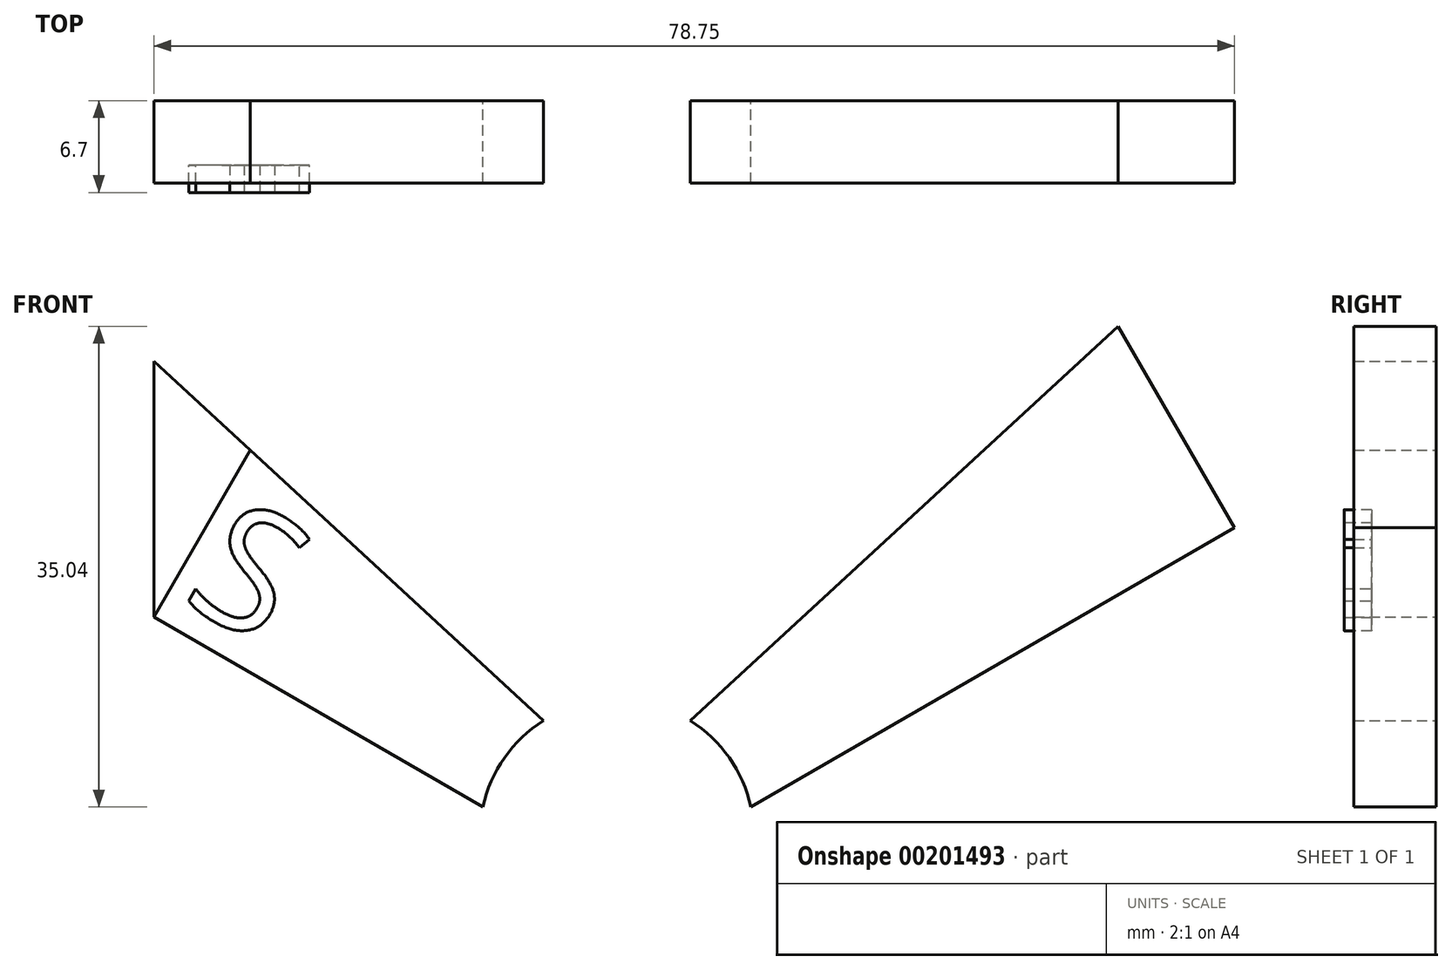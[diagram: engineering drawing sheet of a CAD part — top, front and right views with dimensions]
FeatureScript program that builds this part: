
annotation { "Feature Type Name" : "Feature", "Feature Type Description" : "" }
export const myFeature = defineFeature(function(context is Context, id is Id, definition is map)
    precondition{}
    {
        {
            var Q0;
            Q0=qCreatedBy(makeId("Front.planeOp"),FACE);
            var sketch = newSketch(context, id + "F0", { "sketchPlane" : qUnion([Q0])});
            skCircle(sketch, "E0", {"center": v(0, 0) * mm, "radius": 10 * mm});
            skLineSegment(sketch, "E1.bottom", {"start": v(45, -45) * mm, "end": v(-45, -45) * mm});
            skLineSegment(sketch, "E1.top", {"start": v(45, 45) * mm, "end": v(-45, 45) * mm});
            skLineSegment(sketch, "E1.left", {"start": v(45, -45) * mm, "end": v(45, 45) * mm});
            skLineSegment(sketch, "E1.right", {"start": v(-45, -45) * mm, "end": v(-45, 45) * mm});
            skLineSegment(sketch, "E2", {"start": v(0, 0) * mm, "end": v(-45, 45) * mm, "construction": true});
            skLineSegment(sketch, "E3", {"start": v(0, 0) * mm, "end": v(45, 45) * mm, "construction": true});
            skLineSegment(sketch, "E4", {"start": v(-45, 45) * mm, "end": v(-45, 0) * mm});
            skLineSegment(sketch, "E5", {"start": v(-45, 45) * mm, "end": v(-45, 22.5) * mm});
            skLineSegment(sketch, "E6", {"start": v(0, 0) * mm, "end": v(0, 7) * mm});
            skLineSegment(sketch, "E7", {"start": v(0, 0) * mm, "end": v(0, 3.5) * mm});
            skLineSegment(sketch, "E8", {"start": v(0, 0) * mm, "end": v(0, -3.5) * mm});
            skLineSegment(sketch, "E9", {"start": v(-45, 22.5) * mm, "end": v(0, -3.5) * mm});
            skLineSegment(sketch, "E10", {"start": v(-45, 45) * mm, "end": v(0, 3.5) * mm, "construction": true});
            skLineSegment(sketch, "E11", {"start": v(0, 3.5) * mm, "end": v(45, 45) * mm});
            skLineSegment(sketch, "E12", {"start": v(0, -3.5) * mm, "end": v(45, 22.5) * mm});
            skLineSegment(sketch, "E13", {"start": v(45, 22.5) * mm, "end": v(45, 45) * mm});
            skLineSegment(sketch, "E14", {"start": v(0, 3.5) * mm, "end": v(-45, 45) * mm});
            skLineSegment(sketch, "E15", {"start": v(0, 3.5) * mm, "end": v(-33.75, 34.62) * mm, "construction": true});
            skLineSegment(sketch, "E16", {"start": v(-33.75, 34.62) * mm, "end": v(-33.75, 16) * mm});
            skLineSegment(sketch, "E17", {"start": v(-33.75, 16) * mm, "end": v(-26.73, 28.15) * mm});
            skLineSegment(sketch, "E18", {"start": v(45, 22.5) * mm, "end": v(36.52, 37.18) * mm});
            skSolve(sketch);
        }
        {
            var Q0;
            {var subQ5=sQuery(id+"F0.wireOp",EDGE,"E17");Q0=makeQuery(id+"F0.imprint","IMPRINT",FACE,{"disambiguationData":[TD([[makeQuery(id+"F0.imprint","IMPRINT",EDGE,{"derivedFrom":subQ5}),-1.0]])]});}
            var Q1;
            {var subQ4=sQuery(id+"F0.wireOp",EDGE,"E7");Q1=makeQuery(id+"F0.imprint","IMPRINT",FACE,{"disambiguationData":[TD([[makeQuery(id+"F0.imprint","IMPRINT",EDGE,{"derivedFrom":subQ4}),1.0]])]});}
            var Q2;
            {var subQ5=sQuery(id+"F0.wireOp",EDGE,"E18");Q2=makeQuery(id+"F0.imprint","IMPRINT",FACE,{"disambiguationData":[TD([[makeQuery(id+"F0.imprint","IMPRINT",EDGE,{"derivedFrom":subQ5}),1.0]])]});}
            var Q3;
            {var subQ1=sQuery(id+"F0.wireOp",EDGE,"E7");Q3=makeQuery(id+"F0.imprint","IMPRINT",FACE,{"disambiguationData":[TD([[makeQuery(id+"F0.imprint","IMPRINT",EDGE,{"derivedFrom":subQ1}),-1.0]])]});}
            extrude(context, id + "F1", {"entities" : qUnion([Q0, Q1, Q2, Q3]), "depth" : 6 * mm});
        }
        {
            var Q0;
            Q0=makeQuery(id+"F1.opExtrude","CAP_FACE",FACE,{"disambiguationData":[OSD([sQuery(id+"F0.wireOp",EDGE,"E9"),sQuery(id+"F0.wireOp",EDGE,"E11"),sQuery(id+"F0.wireOp",EDGE,"E12"),sQuery(id+"F0.wireOp",EDGE,"E14"),sQuery(id+"F0.wireOp",EDGE,"E17"),sQuery(id+"F0.wireOp",EDGE,"E18")])],"isStart":false});
            var sketch = newSketch(context, id + "F2", { "sketchPlane" : qUnion([Q0])});
            skText(sketch, "E19", { "text": "S", "fontName": "OpenSans-Regular.ttf"});
            const initialGuessF2  = {"E19": [-0.03444, 0.01897, 1, 0, 0.009]};
            skSetInitialGuess(sketch, initialGuessF2);
            skSolve(sketch);
        }
        {
            var Q0;
            Q0 = qSketchRegion(id + "F2", true);
            extrude(context, id + "F3", {"entities" : qUnion([Q0]), "depth" : 2 * mm});
        }
        {
            var Q0;
            Q0=makeQuery(id+"F3.opExtrude","SWEPT_BODY",BODY,{"disambiguationData":[OSD([sQuery(id+"F2.wireOp",EDGE,"E19.sketch_text.stroke-0"),sQuery(id+"F2.wireOp",EDGE,"E19.sketch_text.stroke-1"),sQuery(id+"F2.wireOp",EDGE,"E19.sketch_text.stroke-2"),sQuery(id+"F2.wireOp",EDGE,"E19.sketch_text.stroke-3"),sQuery(id+"F2.wireOp",EDGE,"E19.sketch_text.stroke-4"),sQuery(id+"F2.wireOp",EDGE,"E19.sketch_text.stroke-5"),sQuery(id+"F2.wireOp",EDGE,"E19.sketch_text.stroke-6"),sQuery(id+"F2.wireOp",EDGE,"E19.sketch_text.stroke-7"),sQuery(id+"F2.wireOp",EDGE,"E19.sketch_text.stroke-8"),sQuery(id+"F2.wireOp",EDGE,"E19.sketch_text.stroke-9"),sQuery(id+"F2.wireOp",EDGE,"E19.sketch_text.stroke-10"),sQuery(id+"F2.wireOp",EDGE,"E19.sketch_text.stroke-11"),sQuery(id+"F2.wireOp",EDGE,"E19.sketch_text.stroke-12"),sQuery(id+"F2.wireOp",EDGE,"E19.sketch_text.stroke-13"),sQuery(id+"F2.wireOp",EDGE,"E19.sketch_text.stroke-14"),sQuery(id+"F2.wireOp",EDGE,"E19.sketch_text.stroke-15"),sQuery(id+"F2.wireOp",EDGE,"E19.sketch_text.stroke-16"),sQuery(id+"F2.wireOp",EDGE,"E19.sketch_text.stroke-17"),sQuery(id+"F2.wireOp",EDGE,"E19.sketch_text.stroke-18"),sQuery(id+"F2.wireOp",EDGE,"E19.sketch_text.stroke-19"),sQuery(id+"F2.wireOp",EDGE,"E19.sketch_text.stroke-20"),sQuery(id+"F2.wireOp",EDGE,"E19.sketch_text.stroke-21"),sQuery(id+"F2.wireOp",EDGE,"E19.sketch_text.stroke-22"),sQuery(id+"F2.wireOp",EDGE,"E19.sketch_text.stroke-23"),sQuery(id+"F2.wireOp",EDGE,"E19.sketch_text.stroke-24")])]});
            var Q1;
            Q1=makeQuery(id+"F1.opExtrude","SWEPT_EDGE",EDGE,{"disambiguationData":[OSD([sQuery(id+"F0.wireOp",EDGE,"E14"),sQuery(id+"F0.wireOp",EDGE,"E17")])]});
            transform(context, id + "F4", {"entities" : qUnion([Q0]), "transformType" : TransformType.ROTATION, "transformAxis" : qUnion([Q1]), "angle" : 30 * degree, "makeCopy" : false});
        }
        {
            var Q0;
            Q0=makeQuery(id+"F3.opExtrude","SWEPT_BODY",BODY,{"disambiguationData":[OSD([sQuery(id+"F2.wireOp",EDGE,"E19.sketch_text.stroke-0"),sQuery(id+"F2.wireOp",EDGE,"E19.sketch_text.stroke-1"),sQuery(id+"F2.wireOp",EDGE,"E19.sketch_text.stroke-2"),sQuery(id+"F2.wireOp",EDGE,"E19.sketch_text.stroke-3"),sQuery(id+"F2.wireOp",EDGE,"E19.sketch_text.stroke-4"),sQuery(id+"F2.wireOp",EDGE,"E19.sketch_text.stroke-5"),sQuery(id+"F2.wireOp",EDGE,"E19.sketch_text.stroke-6"),sQuery(id+"F2.wireOp",EDGE,"E19.sketch_text.stroke-7"),sQuery(id+"F2.wireOp",EDGE,"E19.sketch_text.stroke-8"),sQuery(id+"F2.wireOp",EDGE,"E19.sketch_text.stroke-9"),sQuery(id+"F2.wireOp",EDGE,"E19.sketch_text.stroke-10"),sQuery(id+"F2.wireOp",EDGE,"E19.sketch_text.stroke-11"),sQuery(id+"F2.wireOp",EDGE,"E19.sketch_text.stroke-12"),sQuery(id+"F2.wireOp",EDGE,"E19.sketch_text.stroke-13"),sQuery(id+"F2.wireOp",EDGE,"E19.sketch_text.stroke-14"),sQuery(id+"F2.wireOp",EDGE,"E19.sketch_text.stroke-15"),sQuery(id+"F2.wireOp",EDGE,"E19.sketch_text.stroke-16"),sQuery(id+"F2.wireOp",EDGE,"E19.sketch_text.stroke-17"),sQuery(id+"F2.wireOp",EDGE,"E19.sketch_text.stroke-18"),sQuery(id+"F2.wireOp",EDGE,"E19.sketch_text.stroke-19"),sQuery(id+"F2.wireOp",EDGE,"E19.sketch_text.stroke-20"),sQuery(id+"F2.wireOp",EDGE,"E19.sketch_text.stroke-21"),sQuery(id+"F2.wireOp",EDGE,"E19.sketch_text.stroke-22"),sQuery(id+"F2.wireOp",EDGE,"E19.sketch_text.stroke-23"),sQuery(id+"F2.wireOp",EDGE,"E19.sketch_text.stroke-24")])]});
            transform(context, id + "F5", {"entities" : qUnion([Q0]), "transformType" : TransformType.TRANSLATION_3D, "dx" : 6.1 * mm, "dy" : 1.3 * mm, "dz" : -6.8 * mm, "makeCopy" : false});
        }
        {
            var Q0;
            {var subQ5=sQuery(id+"F0.wireOp",EDGE,"E16");Q0=makeQuery(id+"F0.imprint","IMPRINT",FACE,{"disambiguationData":[TD([[makeQuery(id+"F0.imprint","IMPRINT",EDGE,{"derivedFrom":subQ5}),1.0]])]});}
            var Q1;
            {var subQ4=sQuery(id+"F0.wireOp",EDGE,"E7");Q1=makeQuery(id+"F0.imprint","IMPRINT",FACE,{"disambiguationData":[TD([[makeQuery(id+"F0.imprint","IMPRINT",EDGE,{"derivedFrom":subQ4}),1.0]])]});}
            var Q2;
            {var subQ1=sQuery(id+"F0.wireOp",EDGE,"E7");Q2=makeQuery(id+"F0.imprint","IMPRINT",FACE,{"disambiguationData":[TD([[makeQuery(id+"F0.imprint","IMPRINT",EDGE,{"derivedFrom":subQ1}),-1.0]])]});}
            var Q3;
            {var subQ5=sQuery(id+"F0.wireOp",EDGE,"E13");Q3=makeQuery(id+"F0.imprint","IMPRINT",FACE,{"disambiguationData":[TD([[makeQuery(id+"F0.imprint","IMPRINT",EDGE,{"derivedFrom":subQ5}),1.0]])]});}
            extrude(context, id + "F6", {"entities" : qUnion([Q0, Q1, Q2, Q3]), "depth" : 6 * mm});
        }
    });
